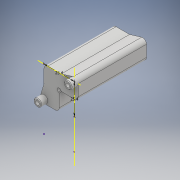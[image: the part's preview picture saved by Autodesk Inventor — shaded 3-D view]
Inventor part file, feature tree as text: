
AUTODESK INVENTOR PART (.ipt)
format: ipt  version: 2018 (Build 220112000, 112)  size: 196,096 bytes
history: native  units: mm
features: sketch x6, extrude x4, chamfer x2, fillet x2, projected_geometry x2, emboss x1
ambient origin geometry x8: Origin, YZ Plane, XZ Plane, XY Plane, X Axis, Y Axis, Z Axis, Center Point
bodies: Solid1 (feature_tree)
feature tree (17):
  sketch  "Sketch1"  dims[d0=30.0mm d2=25.4mm d3=20.0mm d5=25.4mm d8=6.35mm]
  extrude  "Extrusion1"  Depth=25.4mm
  extrude  "Extrusion2"  Depth=12.7mm
  extrude  "Extrusion3"  Depth=57.15mm TaperAngle=0.0deg
  chamfer  "Chamfer1"  Distance=5.588mm
  chamfer  "Chamfer2"  Distance=5.588mm
  fillet  "Fillet1"  Radius=0.5mm
  emboss  "Emboss1"
  fillet  "Fillet2"  Radius=0.5mm
  extrude  "Extrusion4"  Depth=3.175mm
  sketch  "Sketch2"  dims[d11=12.7mm d12=12.7mm]
  sketch  "Sketch3"  dims[d13=11.0mm d14=57.15mm d15=0.0mm]
  sketch  "Sketch4"  dims[d16=6.35mm]
  sketch  "Sketch5"  dims[d17=6.35mm d19=5.588mm d20=0.0mm]
  sketch  "Sketch7"  dims[d21=3.175mm d22=5.588mm d23=0.0mm d24=0.5mm d25=2.0mm d26=45.0deg d27=0.5mm d28=2.0mm d29=45.0deg d30=3.175mm d31=1.5mm d32=0.0mm d36=25.4mm d37=6.35mm d38=11.0mm d39=12.7mm d40=12.7mm d41=3.175mm d42=3.175mm d43=3.175mm d44=0.0mm d45=0.0mm]
  projected_geometry  "Projected Loop2"
  projected_geometry  "Projected Loop3"
